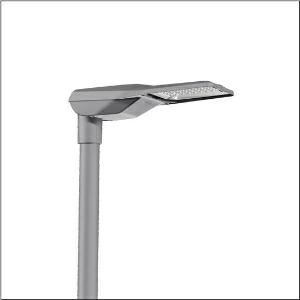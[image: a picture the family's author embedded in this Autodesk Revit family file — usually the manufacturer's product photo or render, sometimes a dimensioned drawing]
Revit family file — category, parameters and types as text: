
# Revit family: streetlight_sl_21_iq_mini___st0_5a_5xe2b31g08hb_4c73
name_source: partatom
category: Lighting Fixtures
units: mm (PartAtom-declared; Revit-internal decimal feet)

## family parameters
Cut with Voids When Loaded = No
Host = Face
Light Source = No
Part Type = Normal
Room Calculation Point = No
Round Connector Dimension = Use Diameter
Shared = No

## types (1)
- --- (1 x LED, 9450 lm, 70.9 W, 3000K)
    Apparent Load = 71 VA
    CIE Flux Codes = 41 75 97 100 100
    Color Rendering = 70
    Color Temperature = 3000K
    Default Elevation = 1800 mm
    Description = Streetlight SL 21 iQ mini, mast luminaire, primary light control with lens, of PMMA, primary optical cover: cover, of toughened safety glass, transparent, light distribution: ST0.5a, light emission: direct distribution, primary light characteristic: asymmetric, installation type: post-top, side-entry, LED, High Power LED, rated luminous flux: 9.450lm, luminous efficacy: 133lm/W, light colour: 730, colour temperature: 3000K, control: Street-Remote, Auto-Match, Temp-Guard, Lumen-Switch, Night-Set, Smart-Wire, Light-Fading, Desk-Remote (wireless, voltage-free reading and setting of iQ features in the workshop via application-optimized NFC function/RFID function), optimised constant luminous flux control (CLO 2.0), presetting dimming linear, mains connection: 220..240V, AC, 50/60Hz, start of lifetime: 71W, end of service life: 75W, reduction: 31W, luminaire housing, of diecast aluminium, powder-coated, Siteco® metallic grey (DB 702S), corrosivity category C5 mid according to DIN EN ISO 12944, please order mast flange separately, inclination adjustable: 0°, 5°, 10°, 15°, sealing non-destructively replaceable, multi-level sealing system, length: 628mm, width: 235mm, height: 110mm, mast flange for spigot size: 42mm (side-entry): 5XC10008XM4, 60/48mm (side-entry/post-top): 5XC10108XM2, 76/60mm (side-entry/post-top): 5XC10108XM1, protection rating (complete): IP66, insulation class (complete): insulation class II (safety insulation), certification: CE, ENEC, ENEC+, VDE, impact resistance: IK09, permissible operating ambient temperature for outdoor applications: -40..+50°C, standard-compliant lighting for roads and squares, packaging unit: 1 piece

Light Distribution: ST0.5a
    Height = 110 mm
    Lamp = 1 x LED
    Lamp Light Flux = 9450 lm
    Lamp Power = 70.9 W
    Lamp count = 1
    Length = 625 mm
    Luminous efficacy = 133 lm/W
    Manufacturer = Siteco
    ModVariant = No
    Model = 5XE2B31G08HB
    Number of Poles = 1
    OnlyDefault = Yes
    Power Factor = 1
    Product Name = Streetlight SL 21 iQ mini | ST0.5a
    Product group = mast luminaire | pylon top
    ProductGroupID = 6100
    Protection Class = Protection class II
    Protection Degree = IP 66
    RLX_Detail_Level = 1
    RLX_Emergency_Light_Flux = 0 lm
    RLX_Emergency_Type = 0
    RLX_Emergency_Type_DB = No
    RlxData = <blob elided: 104461 chars, md5=3575b097>
    Socket = socket
    Standby Power = 0 W
    System Light Flux = 9450 lm
    System Power = 71 W
    Type Comments = factory setting: luminous flux: 100 % | dim-lin: 254 | 711 mA
    Type Image = l_1003519.jpg
    URL = http://relux.com
    VarID = @adj_090913
    Voltage = 0 V
    Weight = 0.00 kg
    Width = 234 mm

## geometry (parser evidence)
native form markers: Blend x4, Sweep x10
no freeform markers — native parametric forms only
